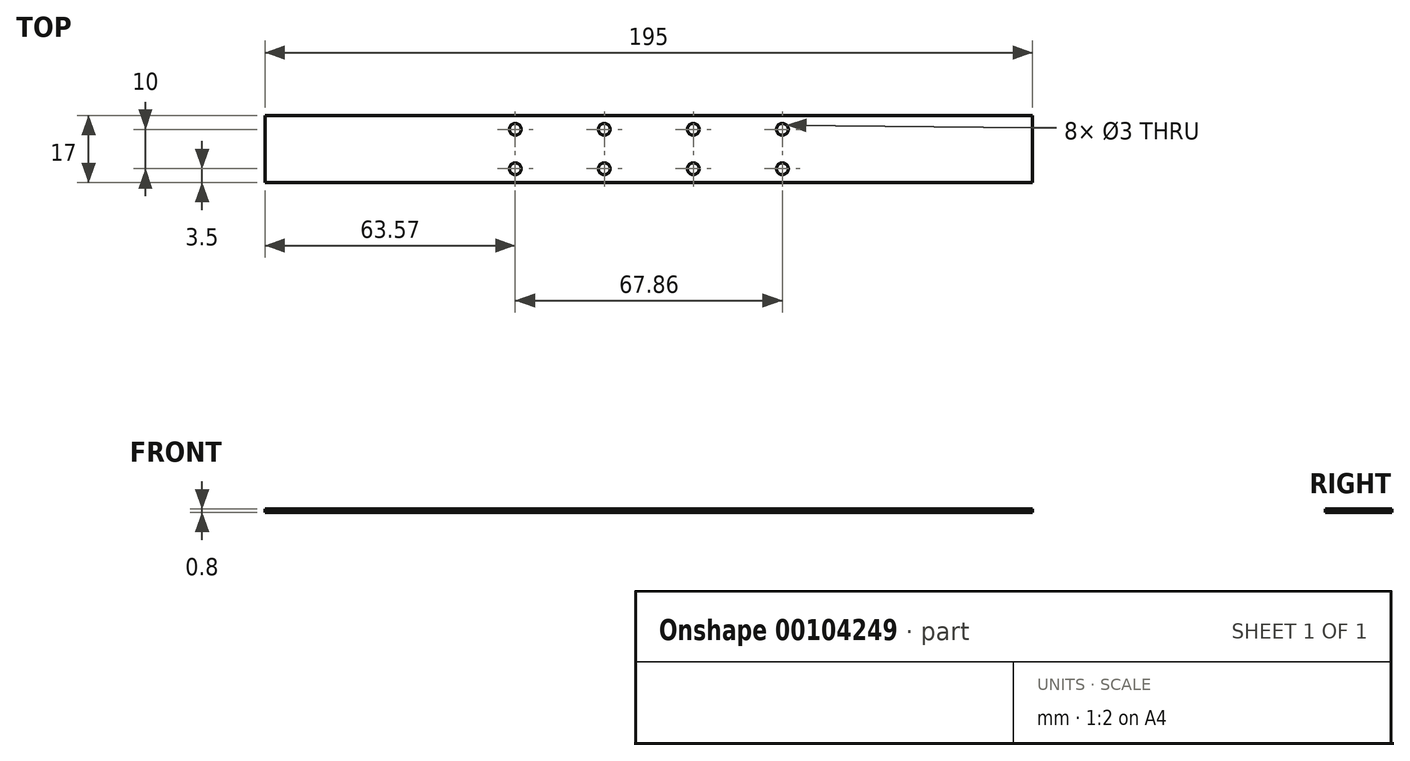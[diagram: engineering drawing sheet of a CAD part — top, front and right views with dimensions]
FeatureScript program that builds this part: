
annotation { "Feature Type Name" : "Feature", "Feature Type Description" : "" }
export const myFeature = defineFeature(function(context is Context, id is Id, definition is map)
    precondition{}
    {
        {
            var Q0;
            Q0=qCreatedBy(makeId("Top.planeOp"),FACE);
            var sketch = newSketch(context, id + "F0", { "sketchPlane" : qUnion([Q0])});
            skLineSegment(sketch, "E0.bottom", {"start": v(0, 17) * mm, "end": v(-95, 17) * mm});
            skLineSegment(sketch, "E0.top", {"start": v(0, 0) * mm, "end": v(-95, 0) * mm});
            skLineSegment(sketch, "E0.left", {"start": v(0, 0) * mm, "end": v(0, 17) * mm});
            skLineSegment(sketch, "E0.right", {"start": v(-95, 0) * mm, "end": v(-95, 17) * mm});
            skCircle(sketch, "E1", {"center": v(-81.43, 3.5) * mm, "radius": 1.5 * mm});
            skCircle(sketch, "E2", {"center": v(-81.43, 13.5) * mm, "radius": 1.5 * mm});
            skCircle(sketch, "E3.1.0.0", {"center": v(-58.81, 13.5) * mm, "radius": 1.5 * mm});
            skCircle(sketch, "E3.1.0.1", {"center": v(-58.81, 3.5) * mm, "radius": 1.5 * mm});
            skCircle(sketch, "E3.2.0.0", {"center": v(-36.19, 13.5) * mm, "radius": 1.5 * mm});
            skCircle(sketch, "E3.2.0.1", {"center": v(-36.19, 3.5) * mm, "radius": 1.5 * mm});
            skCircle(sketch, "E3.3.0.0", {"center": v(-13.57, 13.5) * mm, "radius": 1.5 * mm});
            skCircle(sketch, "E3.3.0.1", {"center": v(-13.57, 3.5) * mm, "radius": 1.5 * mm});
            skLineSegment(sketch, "E3.direction1", {"start": v(-81.43, 13.5) * mm, "end": v(-58.81, 13.5) * mm, "construction": true});
            skLineSegment(sketch, "E4", {"start": v(-81.43, 13.5) * mm, "end": v(-95, 13.5) * mm, "construction": true});
            skLineSegment(sketch, "E5", {"start": v(-13.57, 13.5) * mm, "end": v(0, 13.5) * mm, "construction": true});
            skSolve(sketch);
        }
        {
            var Q0;
            Q0 = qSketchRegion(id + "F0", true);
            extrude(context, id + "F1", {"entities" : qUnion([Q0]), "depth" : 0.8 * mm});
        }
        {
            var Q0;
            Q0=makeQuery(id+"F1.opExtrude","CAP_FACE",FACE,{"disambiguationData":[OSD([sQuery(id+"F0.wireOp",EDGE,"E0.bottom"),sQuery(id+"F0.wireOp",EDGE,"E0.top"),sQuery(id+"F0.wireOp",EDGE,"E0.left"),sQuery(id+"F0.wireOp",EDGE,"E0.right"),sQuery(id+"F0.wireOp",EDGE,"E1"),sQuery(id+"F0.wireOp",EDGE,"E2"),sQuery(id+"F0.wireOp",EDGE,"E3.1.0.0"),sQuery(id+"F0.wireOp",EDGE,"E3.1.0.1"),sQuery(id+"F0.wireOp",EDGE,"E3.2.0.0"),sQuery(id+"F0.wireOp",EDGE,"E3.2.0.1"),sQuery(id+"F0.wireOp",EDGE,"E3.3.0.0"),sQuery(id+"F0.wireOp",EDGE,"E3.3.0.1")])],"isStart":false});
            var sketch = newSketch(context, id + "F2", { "sketchPlane" : qUnion([Q0])});
            skLineSegment(sketch, "E6.bottom", {"start": v(0, 17) * mm, "end": v(50, 17) * mm});
            skLineSegment(sketch, "E6.top", {"start": v(0, 0) * mm, "end": v(50, 0) * mm});
            skLineSegment(sketch, "E6.left", {"start": v(0, 17) * mm, "end": v(0, 0) * mm});
            skLineSegment(sketch, "E6.right", {"start": v(50, 17) * mm, "end": v(50, 0) * mm});
            skLineSegment(sketch, "E7.bottom", {"start": v(-95, 17) * mm, "end": v(-145, 17) * mm});
            skLineSegment(sketch, "E7.top", {"start": v(-95, 0) * mm, "end": v(-145, 0) * mm});
            skLineSegment(sketch, "E7.left", {"start": v(-95, 17) * mm, "end": v(-95, 0) * mm});
            skLineSegment(sketch, "E7.right", {"start": v(-145, 17) * mm, "end": v(-145, 0) * mm});
            skSolve(sketch);
        }
        {
            var Q0;
            Q0 = qSketchRegion(id + "F2", true);
            var Q1;
            Q1=makeQuery(id+"F1.opExtrude","CAP_FACE",FACE,{"disambiguationData":[OSD([sQuery(id+"F0.wireOp",EDGE,"E0.bottom"),sQuery(id+"F0.wireOp",EDGE,"E0.top"),sQuery(id+"F0.wireOp",EDGE,"E0.left"),sQuery(id+"F0.wireOp",EDGE,"E0.right"),sQuery(id+"F0.wireOp",EDGE,"E1"),sQuery(id+"F0.wireOp",EDGE,"E2"),sQuery(id+"F0.wireOp",EDGE,"E3.1.0.0"),sQuery(id+"F0.wireOp",EDGE,"E3.1.0.1"),sQuery(id+"F0.wireOp",EDGE,"E3.2.0.0"),sQuery(id+"F0.wireOp",EDGE,"E3.2.0.1"),sQuery(id+"F0.wireOp",EDGE,"E3.3.0.0"),sQuery(id+"F0.wireOp",EDGE,"E3.3.0.1")])],"isStart":true});
            extrude(context, id + "F3", {"entities" : qUnion([Q0]), "operationType" : NewBodyOperationType.ADD, "endBound" : BoundingType.UP_TO_SURFACE, "oppositeDirection" : true, "endBoundEntityFace" : qUnion([Q1]), "depth" : 25 * mm});
        }
    });
